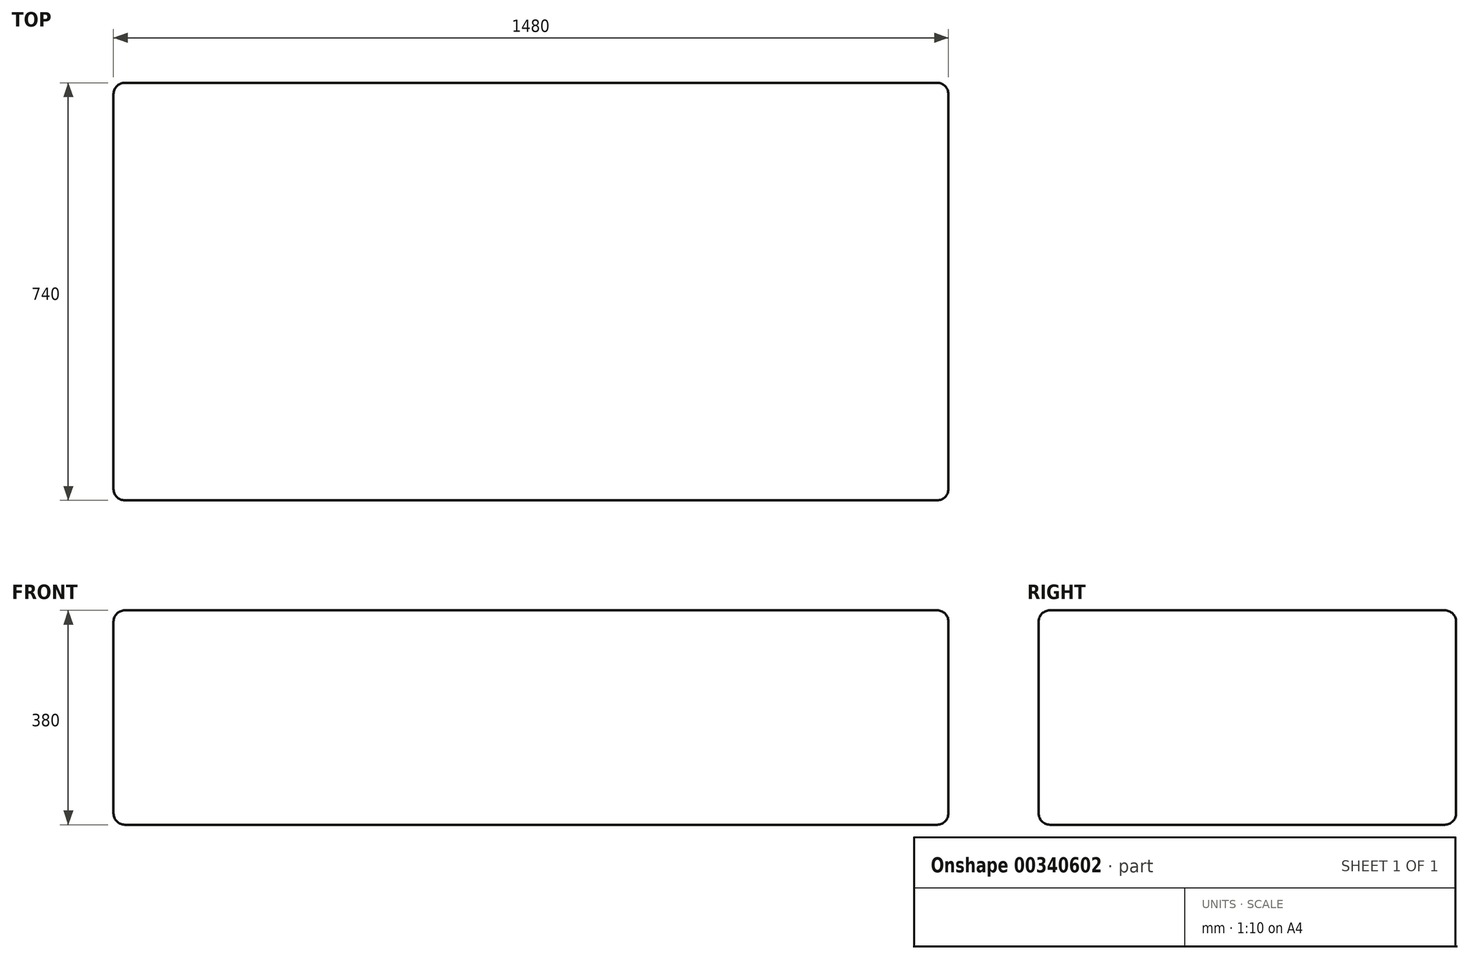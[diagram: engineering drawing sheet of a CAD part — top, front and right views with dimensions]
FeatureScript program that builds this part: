
annotation { "Feature Type Name" : "Feature", "Feature Type Description" : "" }
export const myFeature = defineFeature(function(context is Context, id is Id, definition is map)
    precondition{}
    {
        {
            var Q0;
            Q0=qCreatedBy(makeId("Top.planeOp"),FACE);
            var sketch = newSketch(context, id + "F0", { "sketchPlane" : qUnion([Q0])});
            skLineSegment(sketch, "E0.bottom", {"start": v(-55.84, 693.82) * mm, "end": v(1424.16, 693.82) * mm});
            skLineSegment(sketch, "E0.top", {"start": v(-55.84, -46.18) * mm, "end": v(1424.16, -46.18) * mm});
            skLineSegment(sketch, "E0.left", {"start": v(-55.84, 693.82) * mm, "end": v(-55.84, -46.18) * mm});
            skLineSegment(sketch, "E0.right", {"start": v(1424.16, 693.82) * mm, "end": v(1424.16, -46.18) * mm});
            skSolve(sketch);
        }
        {
            var Q0;
            Q0 = qSketchRegion(id + "F0", true);
            extrude(context, id + "F1", {"entities" : qUnion([Q0]), "depth" : 380 * mm});
        }
        {
            var Q0;
            Q0=makeQuery(id+"F1.opExtrude","SWEPT_EDGE",EDGE,{"disambiguationData":[OSD([sQuery(id+"F0.wireOp",EDGE,"E0.bottom"),sQuery(id+"F0.wireOp",EDGE,"E0.left")])]});
            var Q1;
            Q1=makeQuery(id+"F1.opExtrude","SWEPT_FACE",FACE,{"disambiguationData":[OSD([sQuery(id+"F0.wireOp",EDGE,"E0.bottom")])]});
            var Q2;
            Q2=makeQuery(id+"F1.opExtrude","CAP_FACE",FACE,{"disambiguationData":[OSD([sQuery(id+"F0.wireOp",EDGE,"E0.bottom"),sQuery(id+"F0.wireOp",EDGE,"E0.top"),sQuery(id+"F0.wireOp",EDGE,"E0.left"),sQuery(id+"F0.wireOp",EDGE,"E0.right")])],"isStart":true});
            var Q3;
            Q3=makeQuery(id+"F1.opExtrude","SWEPT_EDGE",EDGE,{"disambiguationData":[OSD([sQuery(id+"F0.wireOp",EDGE,"E0.top"),sQuery(id+"F0.wireOp",EDGE,"E0.left")])]});
            var Q4;
            Q4=makeQuery(id+"F1.opExtrude","CAP_FACE",FACE,{"disambiguationData":[OSD([sQuery(id+"F0.wireOp",EDGE,"E0.bottom"),sQuery(id+"F0.wireOp",EDGE,"E0.top"),sQuery(id+"F0.wireOp",EDGE,"E0.left"),sQuery(id+"F0.wireOp",EDGE,"E0.right")])],"isStart":false});
            var Q5;
            Q5=makeQuery(id+"F1.opExtrude","SWEPT_EDGE",EDGE,{"disambiguationData":[OSD([sQuery(id+"F0.wireOp",EDGE,"E0.top"),sQuery(id+"F0.wireOp",EDGE,"E0.right")])]});
            var Q6;
            Q6=makeQuery(id+"F1.opExtrude","SWEPT_FACE",FACE,{"disambiguationData":[OSD([sQuery(id+"F0.wireOp",EDGE,"E0.top")])]});
            var Q7;
            Q7=makeQuery(id+"F1.opExtrude","SWEPT_FACE",FACE,{"disambiguationData":[OSD([sQuery(id+"F0.wireOp",EDGE,"E0.left")])]});
            var Q8;
            Q8=makeQuery(id+"F1.opExtrude","SWEPT_FACE",FACE,{"disambiguationData":[OSD([sQuery(id+"F0.wireOp",EDGE,"E0.right")])]});
            var Q9;
            Q9=makeQuery(id+"F1.opExtrude","CAP_EDGE",EDGE,{"disambiguationData":[OSD([sQuery(id+"F0.wireOp",EDGE,"E0.left")])],"isStart":false});
            var Q10;
            Q10=makeQuery(id+"F1.opExtrude","SWEPT_EDGE",EDGE,{"disambiguationData":[OSD([sQuery(id+"F0.wireOp",EDGE,"E0.bottom"),sQuery(id+"F0.wireOp",EDGE,"E0.right")])]});
            var Q11;
            Q11=makeQuery(id+"F1.opExtrude","CAP_EDGE",EDGE,{"disambiguationData":[OSD([sQuery(id+"F0.wireOp",EDGE,"E0.bottom")])],"isStart":true});
            var Q12;
            Q12=makeQuery(id+"F1.opExtrude","CAP_EDGE",EDGE,{"disambiguationData":[OSD([sQuery(id+"F0.wireOp",EDGE,"E0.bottom")])],"isStart":false});
            var Q13;
            Q13=makeQuery(id+"F1.opExtrude","CAP_EDGE",EDGE,{"disambiguationData":[OSD([sQuery(id+"F0.wireOp",EDGE,"E0.top")])],"isStart":true});
            var Q14;
            Q14=makeQuery(id+"F1.opExtrude","CAP_EDGE",EDGE,{"disambiguationData":[OSD([sQuery(id+"F0.wireOp",EDGE,"E0.top")])],"isStart":false});
            var Q15;
            Q15=makeQuery(id+"F1.opExtrude","CAP_EDGE",EDGE,{"disambiguationData":[OSD([sQuery(id+"F0.wireOp",EDGE,"E0.left")])],"isStart":true});
            var Q16;
            Q16=makeQuery(id+"F1.opExtrude","CAP_EDGE",EDGE,{"disambiguationData":[OSD([sQuery(id+"F0.wireOp",EDGE,"E0.right")])],"isStart":true});
            var Q17;
            Q17=makeQuery(id+"F1.opExtrude","CAP_EDGE",EDGE,{"disambiguationData":[OSD([sQuery(id+"F0.wireOp",EDGE,"E0.right")])],"isStart":false});
            fillet(context, id + "F2", {"entities" : qUnion([Q0, Q1, Q2, Q3, Q4, Q5, Q6, Q7, Q8, Q9, Q10, Q11, Q12, Q13, Q14, Q15, Q16, Q17]), "radius" : 20 * mm, "tangentPropagation" : true, "allowEdgeOverflow" : false});
        }
    });
